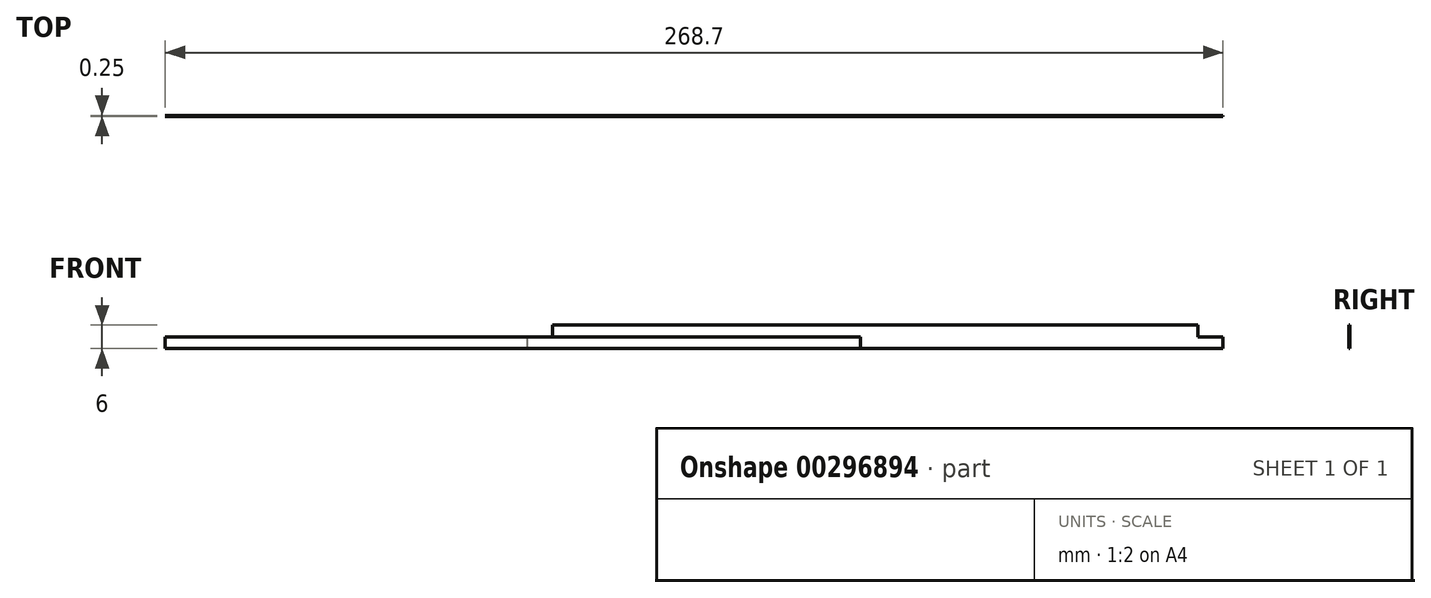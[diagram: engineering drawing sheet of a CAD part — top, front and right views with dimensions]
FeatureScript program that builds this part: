
annotation { "Feature Type Name" : "Feature", "Feature Type Description" : "" }
export const myFeature = defineFeature(function(context is Context, id is Id, definition is map)
    precondition{}
    {
        {
            assignVariable(context, id + "F0", {"name" : "width", "anyValue" : 67 / 406.4 * mm});
        }
        {
            var Q0;
            Q0=qCreatedBy(makeId("Front.planeOp"),FACE);
            var sketch = newSketch(context, id + "F1", { "sketchPlane" : qUnion([Q0])});
            skLineSegment(sketch, "E0.top", {"start": v(-42.26, -4.78) * mm, "end": v(134.35, -4.78) * mm});
            skLineSegment(sketch, "E1", {"start": v(-35.91, 1.22) * mm, "end": v(128, 1.22) * mm});
            skLineSegment(sketch, "E2", {"start": v(-42.26, -4.78) * mm, "end": v(-42.26, -1.78) * mm});
            skLineSegment(sketch, "E3", {"start": v(-35.91, 1.22) * mm, "end": v(-35.91, -39.65) * mm, "construction": true});
            skLineSegment(sketch, "E4", {"start": v(-42.26, -1.78) * mm, "end": v(-35.91, -1.78) * mm});
            skLineSegment(sketch, "E5", {"start": v(-35.91, -1.78) * mm, "end": v(-35.91, 1.22) * mm});
            skLineSegment(sketch, "E6", {"start": v(128, 1.22) * mm, "end": v(128, -63.07) * mm, "construction": true});
            skLineSegment(sketch, "E7", {"start": v(134.35, -4.78) * mm, "end": v(134.35, -1.78) * mm});
            skLineSegment(sketch, "E8", {"start": v(134.35, -1.78) * mm, "end": v(128, -1.78) * mm});
            skLineSegment(sketch, "E9", {"start": v(128, -1.78) * mm, "end": v(128, 1.22) * mm});
            skSolve(sketch);
        }
        {
            var Q0;
            Q0 = qSketchRegion(id + "F1", true);
            extrude(context, id + "F2", {"entities" : qUnion([Q0]), "depth" : getVariable(context, 'width') - 0.4 * mm});
        }
        {
            var Q0;
            Q0=makeQuery(id+"F2.opExtrude","CAP_FACE",FACE,{"disambiguationData":[OSD([sQuery(id+"F1.wireOp",EDGE,"E0.top"),sQuery(id+"F1.wireOp",EDGE,"E1"),sQuery(id+"F1.wireOp",EDGE,"E2"),sQuery(id+"F1.wireOp",EDGE,"E4"),sQuery(id+"F1.wireOp",EDGE,"E5"),sQuery(id+"F1.wireOp",EDGE,"E7"),sQuery(id+"F1.wireOp",EDGE,"E8"),sQuery(id+"F1.wireOp",EDGE,"E9")])],"isStart":false});
            var sketch = newSketch(context, id + "F3", { "sketchPlane" : qUnion([Q0])});
            skLineSegment(sketch, "E10", {"start": v(-42.26, -1.78) * mm, "end": v(134.35, -1.78) * mm});
            skLineSegment(sketch, "E11", {"start": v(134.35, -1.78) * mm, "end": v(134.35, -4.78) * mm});
            skLineSegment(sketch, "E12", {"start": v(134.35, -4.78) * mm, "end": v(-42.26, -4.78) * mm});
            skLineSegment(sketch, "E13", {"start": v(-42.26, -4.78) * mm, "end": v(-42.26, -1.78) * mm});
            skSolve(sketch);
        }
        {
            var Q0;
            Q0 = qSketchRegion(id + "F3", true);
            extrude(context, id + "F4", {"entities" : qUnion([Q0]), "operationType" : NewBodyOperationType.ADD, "depth" : 1 / 101.6 * mm});
        }
        {
            var Q0;
            Q0=makeQuery(id+"F2.opExtrude","CAP_FACE",FACE,{"disambiguationData":[OSD([sQuery(id+"F1.wireOp",EDGE,"E0.top"),sQuery(id+"F1.wireOp",EDGE,"E1"),sQuery(id+"F1.wireOp",EDGE,"E2"),sQuery(id+"F1.wireOp",EDGE,"E4"),sQuery(id+"F1.wireOp",EDGE,"E5"),sQuery(id+"F1.wireOp",EDGE,"E7"),sQuery(id+"F1.wireOp",EDGE,"E8"),sQuery(id+"F1.wireOp",EDGE,"E9")])],"isStart":true});
            var sketch = newSketch(context, id + "F5", { "sketchPlane" : qUnion([Q0])});
            skLineSegment(sketch, "E14", {"start": v(-134.35, -1.78) * mm, "end": v(42.26, -1.78) * mm});
            skLineSegment(sketch, "E15", {"start": v(42.26, -1.78) * mm, "end": v(42.26, -4.78) * mm});
            skLineSegment(sketch, "E16", {"start": v(42.26, -4.78) * mm, "end": v(-134.35, -4.78) * mm});
            skLineSegment(sketch, "E17", {"start": v(-134.35, -4.78) * mm, "end": v(-134.35, -1.78) * mm});
            skSolve(sketch);
        }
        {
            var Q0;
            Q0 = qSketchRegion(id + "F5", true);
            extrude(context, id + "F6", {"entities" : qUnion([Q0]), "operationType" : NewBodyOperationType.ADD, "depth" : 1 / 101.6 * mm});
        }
    });
